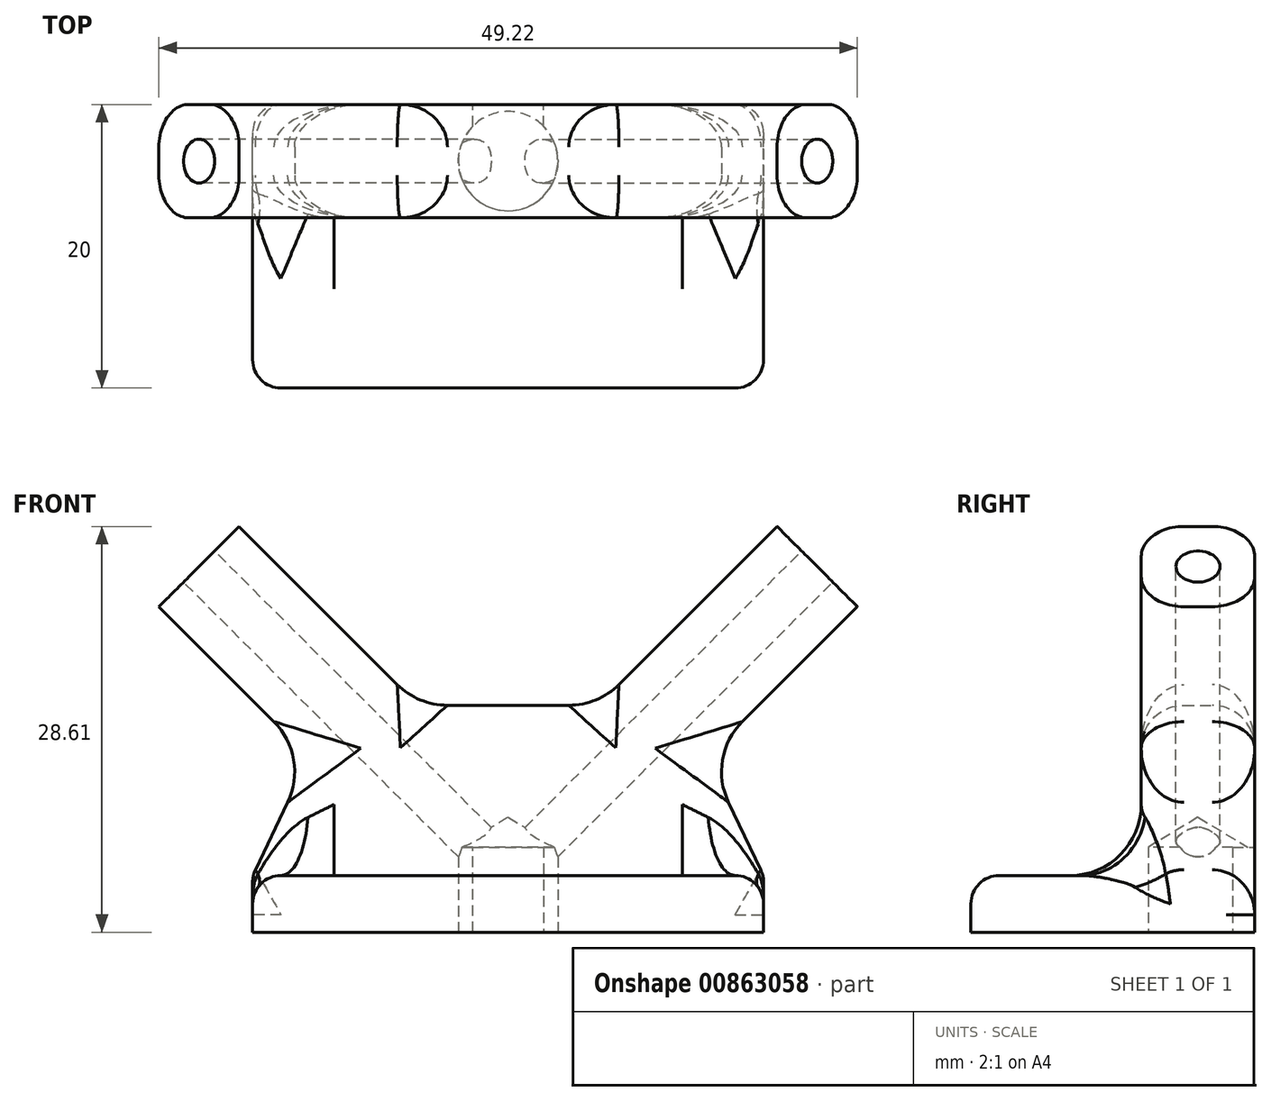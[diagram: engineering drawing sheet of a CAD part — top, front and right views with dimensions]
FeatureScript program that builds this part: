
annotation { "Feature Type Name" : "Feature", "Feature Type Description" : "" }
export const myFeature = defineFeature(function(context is Context, id is Id, definition is map)
    precondition{}
    {
        {
            var Q0;
            Q0=qCreatedBy(makeId("Front.planeOp"),FACE);
            var sketch = newSketch(context, id + "F0", { "sketchPlane" : qUnion([Q0])});
            skLineSegment(sketch, "E0", {"start": v(0, 0) * mm, "end": v(-36.34, 36.34) * mm, "construction": true});
            skLineSegment(sketch, "E1", {"start": v(0, 0) * mm, "end": v(36.34, 36.34) * mm, "construction": true});
            skLineSegment(sketch, "E2", {"start": v(0, 0) * mm, "end": v(-18, 0) * mm});
            skLineSegment(sketch, "E3", {"start": v(-18, 0) * mm, "end": v(-14, 8.34) * mm});
            skLineSegment(sketch, "E4", {"start": v(-14, 8.34) * mm, "end": v(-24.6, 18.95) * mm});
            skLineSegment(sketch, "E5", {"start": v(-24.6, 18.95) * mm, "end": v(-18.95, 24.6) * mm});
            skLineSegment(sketch, "E6", {"start": v(-18.95, 24.6) * mm, "end": v(-6.34, 12) * mm});
            skLineSegment(sketch, "E7", {"start": v(-6.34, 12) * mm, "end": v(0, 12) * mm});
            skLineSegment(sketch, "E8.MirrorCS", {"start": v(6.34, 12) * mm, "end": v(0, 12) * mm});
            skLineSegment(sketch, "E9.MirrorCS", {"start": v(18.95, 24.6) * mm, "end": v(6.34, 12) * mm});
            skLineSegment(sketch, "E10.MirrorCS", {"start": v(24.6, 18.95) * mm, "end": v(18.95, 24.6) * mm});
            skLineSegment(sketch, "E11.MirrorCS", {"start": v(14, 8.34) * mm, "end": v(24.6, 18.95) * mm});
            skLineSegment(sketch, "E12.MirrorCS", {"start": v(18, 0) * mm, "end": v(14, 8.34) * mm});
            skLineSegment(sketch, "E13.MirrorCS", {"start": v(0, 0) * mm, "end": v(18, 0) * mm});
            skSolve(sketch);
        }
        {
            var Q0;
            Q0=makeQuery(id+"F0.imprint","IMPRINT",FACE,{"disambiguationData":[TD([[makeQuery(id+"F0.imprint","IMPRINT",EDGE,{"derivedFrom":sQuery(id+"F0.wireOp",EDGE,"E2")}),-1.0]])]});
            extrude(context, id + "F1", {"entities" : qUnion([Q0]), "depth" : 8 * mm, "offsetDistance" : 25 * mm});
        }
        {
            var Q0;
            Q0=makeQuery(id+"F1.opExtrude","SWEPT_FACE",FACE,{"disambiguationData":[OSD([sQuery(id+"F0.wireOp",EDGE,"E10.MirrorCS")])]});
            var sketch = newSketch(context, id + "F2", { "sketchPlane" : qUnion([Q0])});
            skPoint(sketch, "E14", {"position": v(-4, 0) * mm});
            skPoint(sketch, "E14.positionSnap0", {"position": v(-4, 4) * mm});
            skPoint(sketch, "E14.positionSnap1", {"position": v(0, 0) * mm});
            skSolve(sketch);
        }
        {
            var Q0;
            Q0=makeQuery(id+"F1.opExtrude","SWEPT_FACE",FACE,{"disambiguationData":[OSD([sQuery(id+"F0.wireOp",EDGE,"E5")])]});
            var sketch = newSketch(context, id + "F3", { "sketchPlane" : qUnion([Q0])});
            skPoint(sketch, "E15", {"position": v(4, 0) * mm});
            skPoint(sketch, "E15.positionSnap0", {"position": v(8, 0) * mm});
            skPoint(sketch, "E15.positionSnap1", {"position": v(4, -4) * mm});
            skSolve(sketch);
        }
        {
            var Q0;
            Q0=makeQuery(id+"F1.opExtrude","SWEPT_FACE",FACE,{"disambiguationData":[OSD([sQuery(id+"F0.wireOp",EDGE,"E2"),sQuery(id+"F0.wireOp",EDGE,"E13.MirrorCS")])]});
            var sketch = newSketch(context, id + "F4", { "sketchPlane" : qUnion([Q0])});
            skPoint(sketch, "E16", {"position": v(0, 4) * mm});
            skPoint(sketch, "E16.positionSnap0", {"position": v(-18, 4) * mm});
            skPoint(sketch, "E16.positionSnap1", {"position": v(0, 8) * mm});
            skSolve(sketch);
        }
        {
            var Q0;
            Q0=sQuery(id+"F3.wireOp",VERTEX,"E15");
            var Q1;
            Q1=sQuery(id+"F2.wireOp",VERTEX,"E14");
            var Q2;
            Q2=makeQuery(id+"F1.opExtrude","SWEPT_BODY",BODY,{"disambiguationData":[OSD([sQuery(id+"F0.wireOp",EDGE,"E2"),sQuery(id+"F0.wireOp",EDGE,"E3"),sQuery(id+"F0.wireOp",EDGE,"E4"),sQuery(id+"F0.wireOp",EDGE,"E5"),sQuery(id+"F0.wireOp",EDGE,"E6"),sQuery(id+"F0.wireOp",EDGE,"E7"),sQuery(id+"F0.wireOp",EDGE,"E8.MirrorCS"),sQuery(id+"F0.wireOp",EDGE,"E9.MirrorCS"),sQuery(id+"F0.wireOp",EDGE,"E10.MirrorCS"),sQuery(id+"F0.wireOp",EDGE,"E11.MirrorCS"),sQuery(id+"F0.wireOp",EDGE,"E12.MirrorCS"),sQuery(id+"F0.wireOp",EDGE,"E13.MirrorCS")])]});
            hole(context, id + "F5", {"style" : HoleStyle.SIMPLE, "endStyle" : HoleEndStyle.BLIND, "holeDiameter" : 3.1 * mm, "majorDiameter" : 5 * mm, "holeDepth" : 35 * mm, "isTappedThrough" : true, "tappedDepth" : 12 * mm, "tapClearance" : 3, "locations" : qUnion([Q0, Q1]), "scope" : qUnion([Q2])});
        }
        {
            var Q0;
            {var subQ0=sQuery(id+"F0.wireOp",EDGE,"E2");Q0=makeQuery(id+"F4.imprint","IMPRINT",FACE,{"disambiguationData":[TD([[makeQuery(id+"F4.imprint","IMPRINT",EDGE,{"derivedFrom":makeQuery(id+"F1.opExtrude","SWEPT_EDGE",EDGE,{"disambiguationData":[OSD([subQ0,sQuery(id+"F0.wireOp",EDGE,"E3")])]})}),1.0]])]});}
            var sketch = newSketch(context, id + "F6", { "sketchPlane" : qUnion([Q0])});
            skLineSegment(sketch, "E17", {"start": v(18, 0) * mm, "end": v(18, 20) * mm});
            skLineSegment(sketch, "E18", {"start": v(18, 20) * mm, "end": v(-18, 20) * mm});
            skLineSegment(sketch, "E19", {"start": v(-18, 20) * mm, "end": v(-18, 0) * mm});
            skSolve(sketch);
        }
        {
            var Q0;
            {var subQ2=sQuery(id+"F6.wireOp",EDGE,"E18");Q0=makeQuery(id+"F6.imprint","IMPRINT",FACE,{"disambiguationData":[TD([[makeQuery(id+"F6.imprint","IMPRINT",EDGE,{"derivedFrom":subQ2}),1.0]])]});}
            var Q1;
            {var subQ1=sQuery(id+"F0.wireOp",EDGE,"E13.MirrorCS");var subQ2=sQuery(id+"F0.wireOp",EDGE,"E2");var subQ3=makeQuery(id+"F4.imprint","IMPRINT",EDGE,{"derivedFrom":makeQuery(id+"F1.opExtrude","CAP_EDGE",EDGE,{"disambiguationData":[OSD([subQ2,subQ1])],"isStart":true})});Q1=makeQuery(id+"F6.imprint","IMPRINT",FACE,{"disambiguationData":[TD([[makeQuery(id+"F6.imprint","IMPRINT",EDGE,{"derivedFrom":subQ3}),-1.0]])]});}
            extrude(context, id + "F7", {"entities" : qUnion([Q0, Q1]), "operationType" : NewBodyOperationType.ADD, "depth" : 4 * mm, "offsetDistance" : 25 * mm});
        }
        {
            var Q0;
            Q0=makeQuery(id+"F7.opExtrude","CAP_FACE",FACE,{"disambiguationData":[OSD([sQuery(id+"F0.wireOp",EDGE,"E2"),sQuery(id+"F0.wireOp",EDGE,"E13.MirrorCS"),sQuery(id+"F6.wireOp",EDGE,"E17"),sQuery(id+"F6.wireOp",EDGE,"E18"),sQuery(id+"F6.wireOp",EDGE,"E19")])],"isStart":false});
            var sketch = newSketch(context, id + "F8", { "sketchPlane" : qUnion([Q0])});
            skPoint(sketch, "E20", {"position": v(0, 4) * mm});
            skPoint(sketch, "E20.positionSnap0", {"position": v(0, 0) * mm});
            skSolve(sketch);
        }
        {
            var Q0;
            Q0=sQuery(id+"F8.wireOp",VERTEX,"E20");
            var Q1;
            Q1=makeQuery(id+"F1.opExtrude","SWEPT_BODY",BODY,{"disambiguationData":[OSD([sQuery(id+"F0.wireOp",EDGE,"E2"),sQuery(id+"F0.wireOp",EDGE,"E3"),sQuery(id+"F0.wireOp",EDGE,"E4"),sQuery(id+"F0.wireOp",EDGE,"E5"),sQuery(id+"F0.wireOp",EDGE,"E6"),sQuery(id+"F0.wireOp",EDGE,"E7"),sQuery(id+"F0.wireOp",EDGE,"E8.MirrorCS"),sQuery(id+"F0.wireOp",EDGE,"E9.MirrorCS"),sQuery(id+"F0.wireOp",EDGE,"E10.MirrorCS"),sQuery(id+"F0.wireOp",EDGE,"E11.MirrorCS"),sQuery(id+"F0.wireOp",EDGE,"E12.MirrorCS"),sQuery(id+"F0.wireOp",EDGE,"E13.MirrorCS")])]});
            hole(context, id + "F9", {"style" : HoleStyle.SIMPLE, "endStyle" : HoleEndStyle.BLIND, "holeDiameter" : 7 * mm, "majorDiameter" : 5 * mm, "holeDepth" : 6 * mm, "isTappedThrough" : true, "tappedDepth" : 12 * mm, "tapClearance" : 3, "locations" : qUnion([Q0]), "scope" : qUnion([Q1])});
        }
        {
            var Q0;
            {var subQ0=sQuery(id+"F0.wireOp",EDGE,"E13.MirrorCS");var subQ1=sQuery(id+"F0.wireOp",EDGE,"E2");Q0=makeQuery(id+"F7.boolean.opBoolean","MERGE",FACE,{"derivedFrom":[makeQuery(id+"F1.opExtrude","CAP_FACE",FACE,{"disambiguationData":[OSD([subQ1,sQuery(id+"F0.wireOp",EDGE,"E3"),sQuery(id+"F0.wireOp",EDGE,"E4"),sQuery(id+"F0.wireOp",EDGE,"E5"),sQuery(id+"F0.wireOp",EDGE,"E6"),sQuery(id+"F0.wireOp",EDGE,"E7"),sQuery(id+"F0.wireOp",EDGE,"E8.MirrorCS"),sQuery(id+"F0.wireOp",EDGE,"E9.MirrorCS"),sQuery(id+"F0.wireOp",EDGE,"E10.MirrorCS"),sQuery(id+"F0.wireOp",EDGE,"E11.MirrorCS"),sQuery(id+"F0.wireOp",EDGE,"E12.MirrorCS"),subQ0])],"isStart":true}),makeQuery(id+"F7.opExtrude","SWEPT_FACE",FACE,{"disambiguationData":[OSD([subQ1,subQ0])]})]});}
            var sketch = newSketch(context, id + "F10", { "sketchPlane" : qUnion([Q0])});
            skLineSegment(sketch, "E21", {"start": v(2.5, -4) * mm, "end": v(2.5, 2) * mm});
            skLineSegment(sketch, "E22", {"start": v(2.5, 2) * mm, "end": v(-2.5, 2) * mm});
            skLineSegment(sketch, "E23", {"start": v(-2.5, 2) * mm, "end": v(-2.5, -4) * mm});
            skLineSegment(sketch, "E24", {"start": v(-2.5, -4) * mm, "end": v(2.5, -4) * mm});
            skSolve(sketch);
        }
        {
            var Q0;
            Q0=makeQuery(id+"F10.imprint","IMPRINT",FACE,{"disambiguationData":[TD([[makeQuery(id+"F10.imprint","IMPRINT",EDGE,{"derivedFrom":sQuery(id+"F10.wireOp",EDGE,"E21")}),1.0]])]});
            extrude(context, id + "F11", {"entities" : qUnion([Q0]), "operationType" : NewBodyOperationType.REMOVE, "oppositeDirection" : true, "depth" : 5 * mm, "offsetDistance" : 25 * mm});
        }
        {
            var Q0;
            Q0=makeQuery(id+"F1.opExtrude","CAP_EDGE",EDGE,{"disambiguationData":[OSD([sQuery(id+"F0.wireOp",EDGE,"E6")])],"isStart":false});
            var Q1;
            Q1=makeQuery(id+"F1.opExtrude","CAP_EDGE",EDGE,{"disambiguationData":[OSD([sQuery(id+"F0.wireOp",EDGE,"E7"),sQuery(id+"F0.wireOp",EDGE,"E8.MirrorCS")])],"isStart":false});
            var Q2;
            Q2=makeQuery(id+"F1.opExtrude","CAP_EDGE",EDGE,{"disambiguationData":[OSD([sQuery(id+"F0.wireOp",EDGE,"E9.MirrorCS")])],"isStart":false});
            var Q3;
            Q3=makeQuery(id+"F1.opExtrude","CAP_EDGE",EDGE,{"disambiguationData":[OSD([sQuery(id+"F0.wireOp",EDGE,"E9.MirrorCS")])],"isStart":true});
            var Q4;
            Q4=makeQuery(id+"F1.opExtrude","CAP_EDGE",EDGE,{"disambiguationData":[OSD([sQuery(id+"F0.wireOp",EDGE,"E7"),sQuery(id+"F0.wireOp",EDGE,"E8.MirrorCS")])],"isStart":true});
            var Q5;
            Q5=makeQuery(id+"F1.opExtrude","CAP_EDGE",EDGE,{"disambiguationData":[OSD([sQuery(id+"F0.wireOp",EDGE,"E6")])],"isStart":true});
            var Q6;
            Q6=makeQuery(id+"F1.opExtrude","CAP_EDGE",EDGE,{"disambiguationData":[OSD([sQuery(id+"F0.wireOp",EDGE,"E11.MirrorCS")])],"isStart":true});
            var Q7;
            Q7=makeQuery(id+"F1.opExtrude","CAP_EDGE",EDGE,{"disambiguationData":[OSD([sQuery(id+"F0.wireOp",EDGE,"E11.MirrorCS")])],"isStart":false});
            var Q8;
            Q8=makeQuery(id+"F1.opExtrude","CAP_EDGE",EDGE,{"disambiguationData":[OSD([sQuery(id+"F0.wireOp",EDGE,"E4")])],"isStart":false});
            var Q9;
            Q9=makeQuery(id+"F1.opExtrude","CAP_EDGE",EDGE,{"disambiguationData":[OSD([sQuery(id+"F0.wireOp",EDGE,"E4")])],"isStart":true});
            var Q10;
            Q10=makeQuery(id+"F1.opExtrude","CAP_EDGE",EDGE,{"disambiguationData":[OSD([sQuery(id+"F0.wireOp",EDGE,"E3")])],"isStart":true});
            var Q11;
            Q11=makeQuery(id+"F1.opExtrude","CAP_EDGE",EDGE,{"disambiguationData":[OSD([sQuery(id+"F0.wireOp",EDGE,"E3")])],"isStart":false});
            var Q12;
            Q12=makeQuery(id+"F1.opExtrude","CAP_EDGE",EDGE,{"disambiguationData":[OSD([sQuery(id+"F0.wireOp",EDGE,"E12.MirrorCS")])],"isStart":false});
            var Q13;
            Q13=makeQuery(id+"F1.opExtrude","CAP_EDGE",EDGE,{"disambiguationData":[OSD([sQuery(id+"F0.wireOp",EDGE,"E12.MirrorCS")])],"isStart":true});
            fillet(context, id + "F12", {"entities" : qUnion([Q0, Q1, Q2, Q3, Q4, Q5, Q6, Q7, Q8, Q9, Q10, Q11, Q12, Q13]), "radius" : 3 * mm, "tangentPropagation" : true, "allowEdgeOverflow" : false});
        }
        {
            var Q0;
            Q0=makeQuery(id+"F7.opExtrude","SWEPT_EDGE",EDGE,{"disambiguationData":[OSD([sQuery(id+"F6.wireOp",EDGE,"E18"),sQuery(id+"F6.wireOp",EDGE,"E19")])]});
            var Q1;
            Q1=makeQuery(id+"F7.opExtrude","SWEPT_EDGE",EDGE,{"disambiguationData":[OSD([sQuery(id+"F6.wireOp",EDGE,"E17"),sQuery(id+"F6.wireOp",EDGE,"E18")])]});
            var Q2;
            {var subQ0=makeQuery(id+"F7.opExtrude","CAP_EDGE",EDGE,{"disambiguationData":[OSD([sQuery(id+"F6.wireOp",EDGE,"E19")])],"isStart":true});Q2=makeQuery(id+"F12.opFillet","MERGE",EDGE,{"derivedFrom":[makeQuery(id+"F7.boolean.opBoolean","MERGE",EDGE,{"derivedFrom":[makeQuery(id+"F1.opExtrude","SWEPT_EDGE",EDGE,{"disambiguationData":[OSD([sQuery(id+"F0.wireOp",EDGE,"E2"),sQuery(id+"F0.wireOp",EDGE,"E3")])]}),subQ0]}),makeQuery(id+"F7.boolean.opBoolean","SPLIT",EDGE,{"derivedFrom":subQ0})]});}
            var Q3;
            Q3=makeQuery(id+"F7.opExtrude","CAP_EDGE",EDGE,{"disambiguationData":[OSD([sQuery(id+"F6.wireOp",EDGE,"E18")])],"isStart":true});
            var Q4;
            {var subQ0=makeQuery(id+"F7.opExtrude","CAP_EDGE",EDGE,{"disambiguationData":[OSD([sQuery(id+"F6.wireOp",EDGE,"E17")])],"isStart":true});Q4=makeQuery(id+"F12.opFillet","MERGE",EDGE,{"derivedFrom":[makeQuery(id+"F7.boolean.opBoolean","MERGE",EDGE,{"derivedFrom":[makeQuery(id+"F1.opExtrude","SWEPT_EDGE",EDGE,{"disambiguationData":[OSD([sQuery(id+"F0.wireOp",EDGE,"E12.MirrorCS"),sQuery(id+"F0.wireOp",EDGE,"E13.MirrorCS")])]}),subQ0]}),makeQuery(id+"F7.boolean.opBoolean","SPLIT",EDGE,{"derivedFrom":subQ0})]});}
            fillet(context, id + "F13", {"entities" : qUnion([Q0, Q1, Q2, Q3, Q4]), "radius" : 2 * mm, "tangentPropagation" : true, "allowEdgeOverflow" : false});
        }
        {
            var Q0;
            Q0=makeQuery(id+"F1.opExtrude","CAP_EDGE",EDGE,{"disambiguationData":[OSD([sQuery(id+"F0.wireOp",EDGE,"E2"),sQuery(id+"F0.wireOp",EDGE,"E13.MirrorCS")])],"isStart":false});
            var Q1;
            Q1=makeQuery(id+"F1.opExtrude","SWEPT_EDGE",EDGE,{"disambiguationData":[OSD([sQuery(id+"F0.wireOp",EDGE,"E11.MirrorCS"),sQuery(id+"F0.wireOp",EDGE,"E12.MirrorCS")])]});
            var Q2;
            Q2=makeQuery(id+"F1.opExtrude","SWEPT_EDGE",EDGE,{"disambiguationData":[OSD([sQuery(id+"F0.wireOp",EDGE,"E3"),sQuery(id+"F0.wireOp",EDGE,"E4")])]});
            var Q3;
            Q3=makeQuery(id+"F1.opExtrude","SWEPT_EDGE",EDGE,{"disambiguationData":[OSD([sQuery(id+"F0.wireOp",EDGE,"E8.MirrorCS"),sQuery(id+"F0.wireOp",EDGE,"E9.MirrorCS")])]});
            var Q4;
            Q4=makeQuery(id+"F1.opExtrude","SWEPT_EDGE",EDGE,{"disambiguationData":[OSD([sQuery(id+"F0.wireOp",EDGE,"E6"),sQuery(id+"F0.wireOp",EDGE,"E7")])]});
            fillet(context, id + "F14", {"entities" : qUnion([Q0, Q1, Q2, Q3, Q4]), "radius" : 5 * mm, "tangentPropagation" : true, "allowEdgeOverflow" : false});
        }
    });
